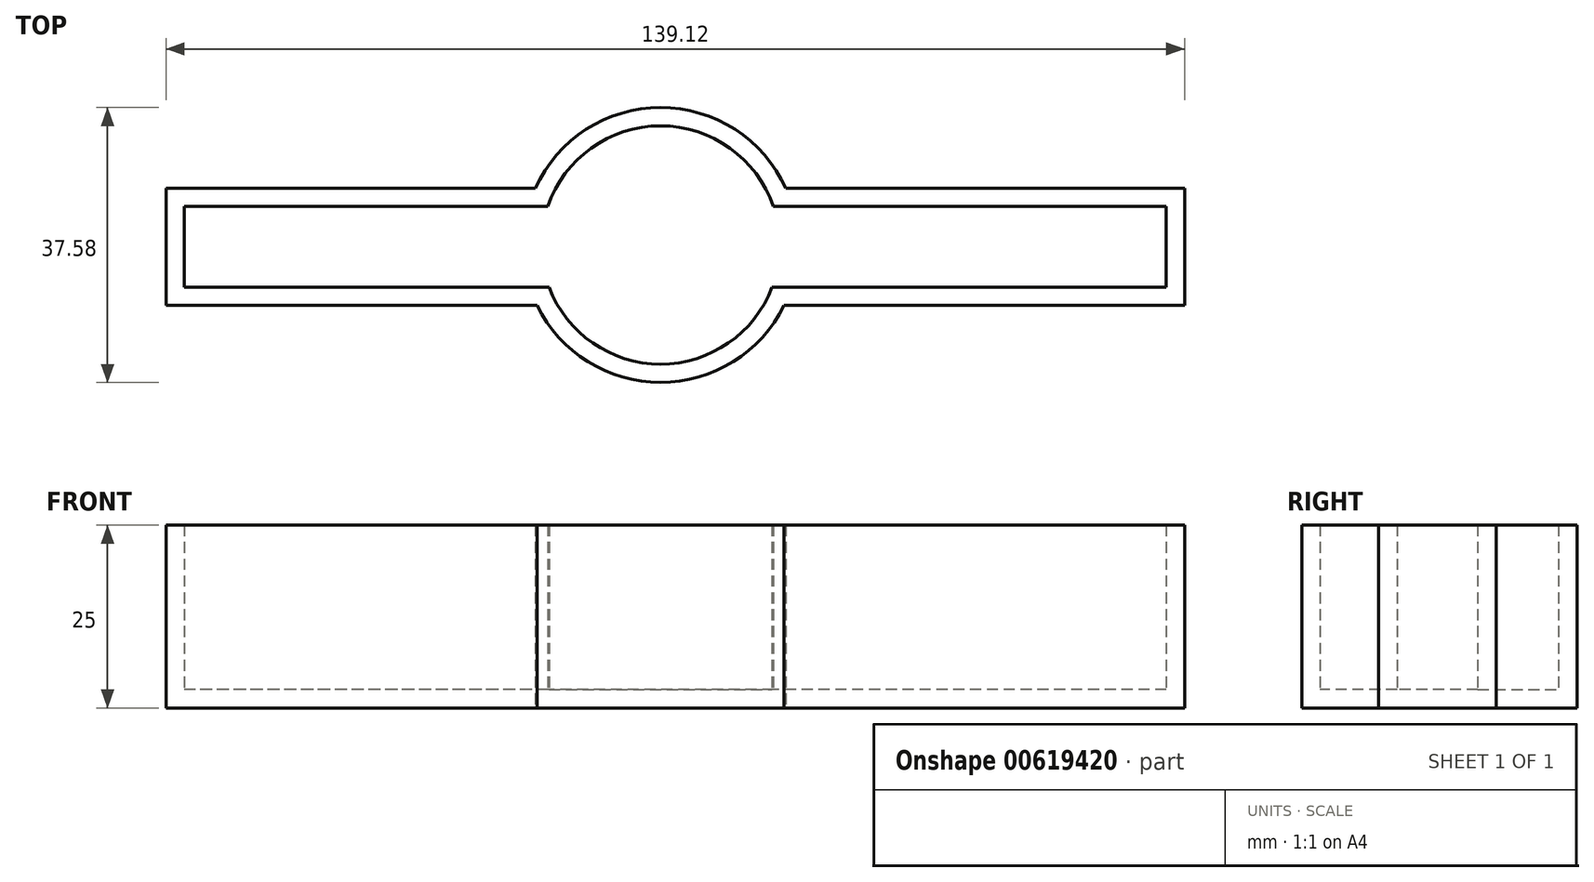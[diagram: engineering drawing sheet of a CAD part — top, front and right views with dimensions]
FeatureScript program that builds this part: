
annotation { "Feature Type Name" : "Feature", "Feature Type Description" : "" }
export const myFeature = defineFeature(function(context is Context, id is Id, definition is map)
    precondition{}
    {
        {
            var Q0;
            Q0=qCreatedBy(makeId("Top.planeOp"),FACE);
            var sketch = newSketch(context, id + "F0", { "sketchPlane" : qUnion([Q0])});
            skCircle(sketch, "E0", {"center": v(0, 0) * mm, "radius": 18.79 * mm});
            skLineSegment(sketch, "E1.bottom", {"start": v(71.58, 7.76) * mm, "end": v(-67.54, 7.76) * mm});
            skLineSegment(sketch, "E1.top", {"start": v(71.58, -8.26) * mm, "end": v(-67.54, -8.26) * mm});
            skLineSegment(sketch, "E1.left", {"start": v(71.58, 7.76) * mm, "end": v(71.58, -8.26) * mm});
            skLineSegment(sketch, "E1.right", {"start": v(-67.54, 7.76) * mm, "end": v(-67.54, -8.26) * mm});
            skSolve(sketch);
        }
        {
            var Q0;
            {var subQ0=sQuery(id+"F0.wireOp",EDGE,"E1.bottom");var subQ1=sQuery(id+"F0.wireOp",EDGE,"E0");var subQ2=makeQuery(id+"F0.imprint","INTERSECT",VERTEX,{"disambiguationData":[OD(0.0)],"derivedFrom":[subQ1,subQ0]});Q0=makeQuery(id+"F0.imprint","IMPRINT",FACE,{"disambiguationData":[TD([[makeQuery(id+"F0.imprint","IMPRINT",EDGE,{"disambiguationData":[TD([[subQ2,1.0]])],"derivedFrom":subQ1}),1.0]])]});}
            var Q1;
            {var subQ5=sQuery(id+"F0.wireOp",EDGE,"E1.right");Q1=makeQuery(id+"F0.imprint","IMPRINT",FACE,{"disambiguationData":[TD([[makeQuery(id+"F0.imprint","IMPRINT",EDGE,{"derivedFrom":subQ5}),1.0]])]});}
            var Q2;
            {var subQ0=sQuery(id+"F0.wireOp",EDGE,"E1.bottom");var subQ1=sQuery(id+"F0.wireOp",EDGE,"E0");var subQ2=makeQuery(id+"F0.imprint","INTERSECT",VERTEX,{"disambiguationData":[OD(0.0)],"derivedFrom":[subQ1,subQ0]});Q2=makeQuery(id+"F0.imprint","IMPRINT",FACE,{"disambiguationData":[TD([[makeQuery(id+"F0.imprint","IMPRINT",EDGE,{"disambiguationData":[TD([[subQ2,-1.0]])],"derivedFrom":subQ1}),1.0]])]});}
            var Q3;
            {var subQ5=sQuery(id+"F0.wireOp",EDGE,"E1.left");Q3=makeQuery(id+"F0.imprint","IMPRINT",FACE,{"disambiguationData":[TD([[makeQuery(id+"F0.imprint","IMPRINT",EDGE,{"derivedFrom":subQ5}),-1.0]])]});}
            var Q4;
            {var subQ0=sQuery(id+"F0.wireOp",EDGE,"E1.top");var subQ1=sQuery(id+"F0.wireOp",EDGE,"E0");var subQ2=makeQuery(id+"F0.imprint","INTERSECT",VERTEX,{"disambiguationData":[OD(0.0)],"derivedFrom":[subQ1,subQ0]});Q4=makeQuery(id+"F0.imprint","IMPRINT",FACE,{"disambiguationData":[TD([[makeQuery(id+"F0.imprint","IMPRINT",EDGE,{"disambiguationData":[TD([[subQ2,-1.0]])],"derivedFrom":subQ1}),1.0]])]});}
            extrude(context, id + "F1", {"entities" : qUnion([Q0, Q1, Q2, Q3, Q4]), "depth" : 25 * mm, "offsetDistance" : 25 * mm});
        }
        {
            var Q0;
            Q0=makeQuery(id+"F1.opExtrude","CAP_FACE",FACE,{"disambiguationData":[OSD([sQuery(id+"F0.wireOp",EDGE,"E0"),sQuery(id+"F0.wireOp",EDGE,"E1.bottom"),sQuery(id+"F0.wireOp",EDGE,"E1.top"),sQuery(id+"F0.wireOp",EDGE,"E1.left"),sQuery(id+"F0.wireOp",EDGE,"E1.right")])],"isStart":false});
            shell(context, id + "F2", {"entities" : qUnion([Q0]), "thickness" : 2.5 * mm});
        }
    });
